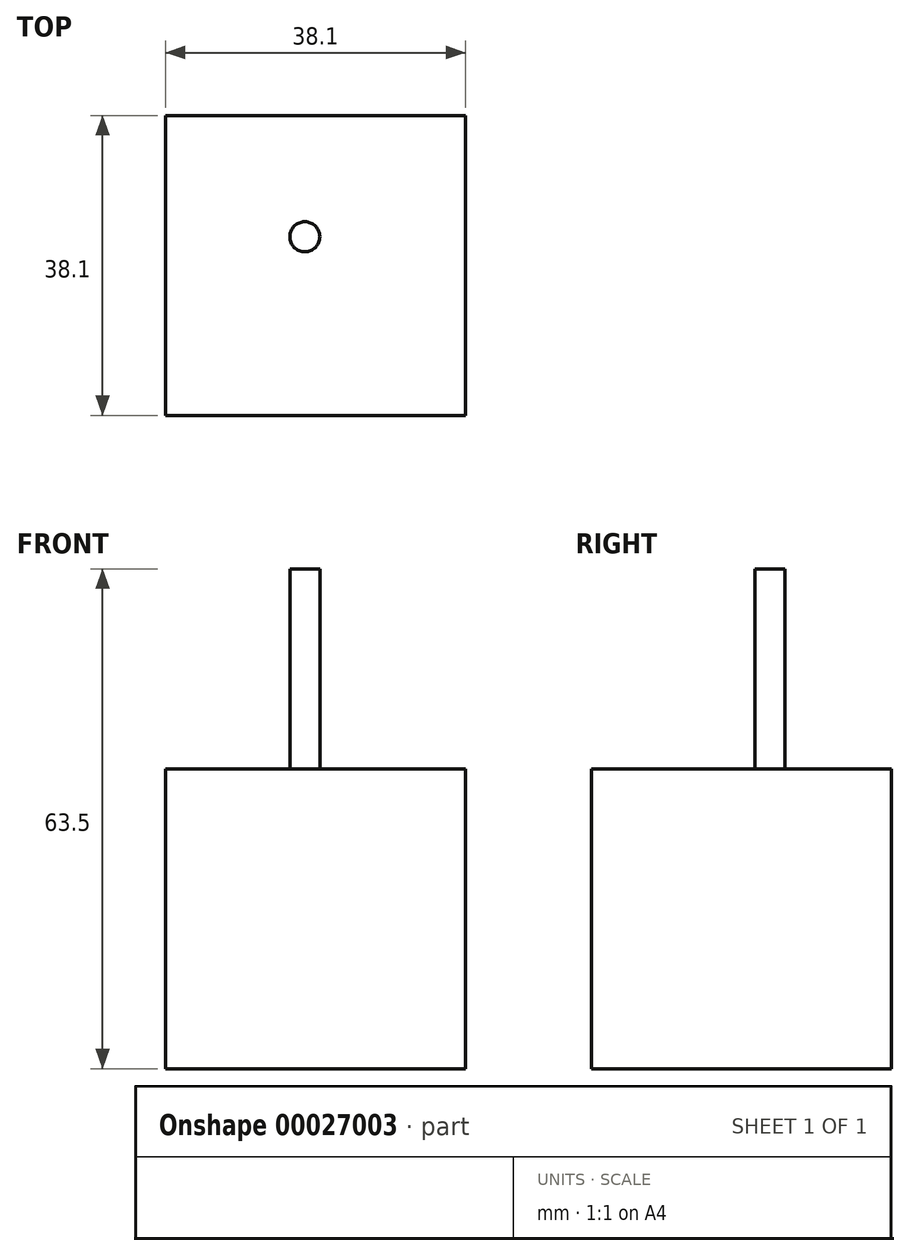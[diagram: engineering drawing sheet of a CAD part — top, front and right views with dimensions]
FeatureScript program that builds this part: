
annotation { "Feature Type Name" : "Feature", "Feature Type Description" : "" }
export const myFeature = defineFeature(function(context is Context, id is Id, definition is map)
    precondition{}
    {
        {
            var Q0;
            Q0=qCreatedBy(makeId("Top.planeOp"),FACE);
            var sketch = newSketch(context, id + "F0", { "sketchPlane" : qUnion([Q0])});
            skLineSegment(sketch, "E0.bottom", {"start": v(0, 0) * mm, "end": v(38.1, 0) * mm});
            skLineSegment(sketch, "E0.top", {"start": v(0, 38.1) * mm, "end": v(38.1, 38.1) * mm});
            skLineSegment(sketch, "E0.left", {"start": v(0, 0) * mm, "end": v(0, 38.1) * mm});
            skLineSegment(sketch, "E0.right", {"start": v(38.1, 0) * mm, "end": v(38.1, 38.1) * mm});
            skSolve(sketch);
        }
        {
            var Q0;
            Q0=makeQuery(id+"F0.imprint","IMPRINT",FACE,{"disambiguationData":[TD([[makeQuery(id+"F0.imprint","IMPRINT",EDGE,{"derivedFrom":sQuery(id+"F0.wireOp",EDGE,"E0.bottom")}),1.0]])]});
            extrude(context, id + "F1", {"entities" : qUnion([Q0]), "depth" : 38.1 * mm});
        }
        {
            var Q0;
            Q0=makeQuery(id+"F1.opExtrude","CAP_FACE",FACE,{"disambiguationData":[OSD([sQuery(id+"F0.wireOp",EDGE,"E0.bottom"),sQuery(id+"F0.wireOp",EDGE,"E0.top"),sQuery(id+"F0.wireOp",EDGE,"E0.left"),sQuery(id+"F0.wireOp",EDGE,"E0.right")])],"isStart":false});
            var sketch = newSketch(context, id + "F2", { "sketchPlane" : qUnion([Q0])});
            skCircle(sketch, "E1", {"center": v(17.69, 22.68) * mm, "radius": 1.9 * mm});
            skSolve(sketch);
        }
        {
            var Q0;
            Q0=makeQuery(id+"F2.imprint","IMPRINT",FACE,{"disambiguationData":[TD([[makeQuery(id+"F2.imprint","IMPRINT",EDGE,{"derivedFrom":sQuery(id+"F2.wireOp",EDGE,"E1")}),1.0]])]});
            var Q1;
            Q1=sQuery(id+"F2.wireOp",EDGE,"E1");
            extrude(context, id + "F3", {"entities" : qUnion([Q0]), "surfaceEntities" : qUnion([Q1]), "depth" : 25.4 * mm});
        }
    });
